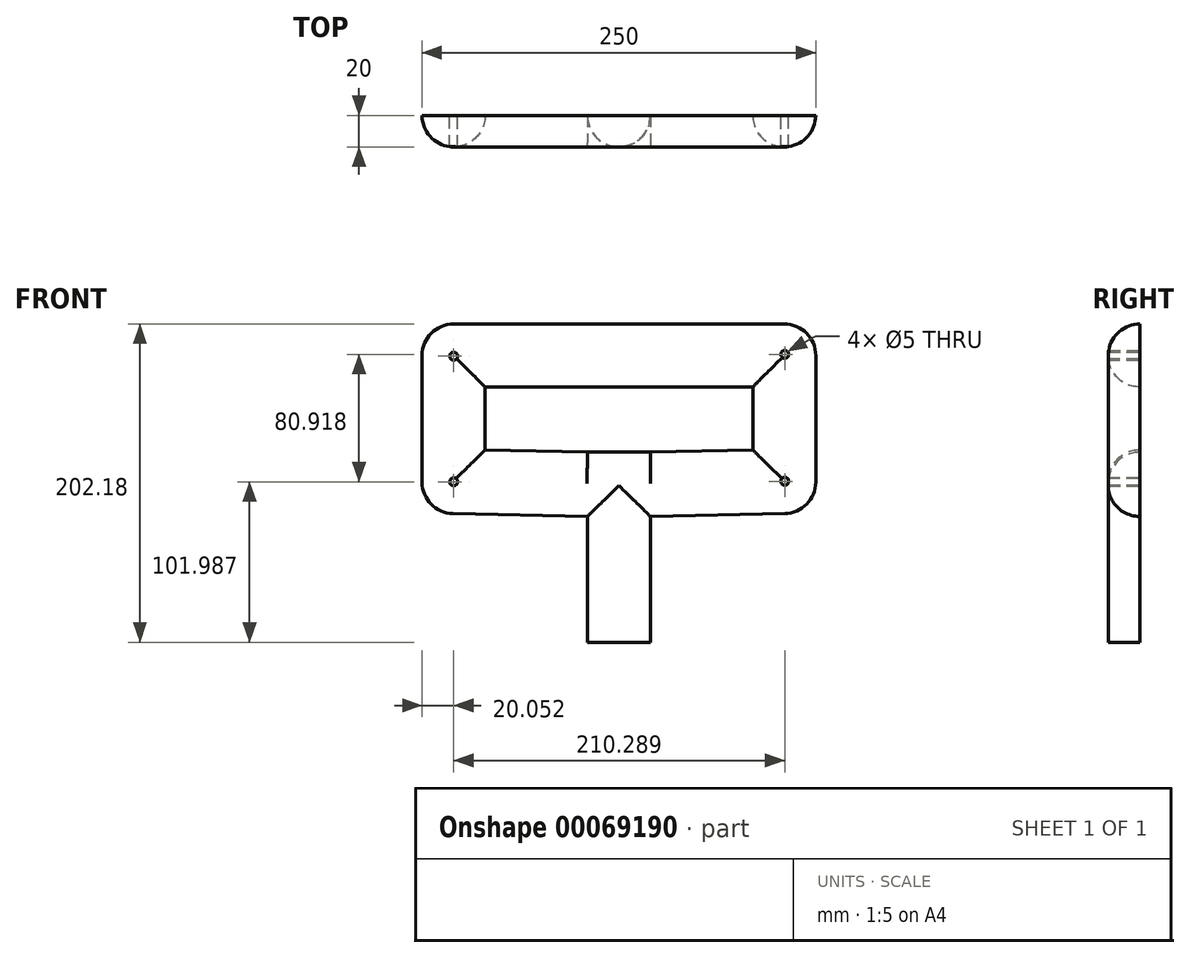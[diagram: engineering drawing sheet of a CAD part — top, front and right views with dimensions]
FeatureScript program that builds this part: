
annotation { "Feature Type Name" : "Feature", "Feature Type Description" : "" }
export const myFeature = defineFeature(function(context is Context, id is Id, definition is map)
    precondition{}
    {
        {
            var Q0;
            Q0=qCreatedBy(makeId("Front.planeOp"),FACE);
            var sketch = newSketch(context, id + "F0", { "sketchPlane" : qUnion([Q0])});
            skLineSegment(sketch, "E0", {"start": v(105, 80) * mm, "end": v(105, 0) * mm});
            skLineSegment(sketch, "E1", {"start": v(105, 0) * mm, "end": v(145, 0) * mm});
            skLineSegment(sketch, "E2", {"start": v(145, 0) * mm, "end": v(145, 80) * mm});
            skLineSegment(sketch, "E3", {"start": v(145, 80) * mm, "end": v(250, 82.18) * mm});
            skLineSegment(sketch, "E4", {"start": v(250, 82.18) * mm, "end": v(250, 202.18) * mm});
            skLineSegment(sketch, "E5", {"start": v(250, 202.18) * mm, "end": v(0, 202.18) * mm});
            skLineSegment(sketch, "E6", {"start": v(0, 202.18) * mm, "end": v(0, 82.18) * mm});
            skLineSegment(sketch, "E7", {"start": v(0, 82.18) * mm, "end": v(105, 80) * mm});
            skLineSegment(sketch, "E8", {"start": v(40, 162.18) * mm, "end": v(40, 122.18) * mm});
            skLineSegment(sketch, "E9", {"start": v(40, 122.18) * mm, "end": v(105, 120.83) * mm});
            skLineSegment(sketch, "E10", {"start": v(105, 120.83) * mm, "end": v(145, 120.83) * mm});
            skLineSegment(sketch, "E11", {"start": v(145, 120.83) * mm, "end": v(210, 122.18) * mm});
            skLineSegment(sketch, "E12", {"start": v(210, 122.18) * mm, "end": v(210, 162.18) * mm});
            skLineSegment(sketch, "E13", {"start": v(210, 162.18) * mm, "end": v(40, 162.18) * mm});
            skLineSegment(sketch, "E14", {"start": v(105, 80) * mm, "end": v(105, 120.83) * mm, "construction": true});
            skLineSegment(sketch, "E15", {"start": v(145, 80) * mm, "end": v(145, 120.83) * mm, "construction": true});
            skLineSegment(sketch, "E16", {"start": v(105, 80) * mm, "end": v(145, 80) * mm, "construction": true});
            skPoint(sketch, "E17", {"position": v(125, 162.18) * mm});
            skLineSegment(sketch, "E18", {"start": v(0, 82.18) * mm, "end": v(0, 0) * mm});
            skPoint(sketch, "E19", {"position": v(125, 202.18) * mm});
            skPoint(sketch, "E20", {"position": v(40, 142.18) * mm});
            skPoint(sketch, "E21", {"position": v(0, 142.18) * mm});
            skSolve(sketch);
        }
        {
            var Q0;
            Q0 = qSketchRegion(id + "F0", true);
            extrude(context, id + "F1", {"entities" : qUnion([Q0]), "depth" : 20 * mm});
        }
        {
            var Q0;
            Q0=makeQuery(id+"F1.opExtrude","CAP_EDGE",EDGE,{"disambiguationData":[OSD([sQuery(id+"F0.wireOp",EDGE,"E4")])],"isStart":false});
            var Q1;
            Q1=makeQuery(id+"F1.opExtrude","CAP_EDGE",EDGE,{"disambiguationData":[OSD([sQuery(id+"F0.wireOp",EDGE,"E6")])],"isStart":false});
            var Q2;
            Q2=makeQuery(id+"F1.opExtrude","CAP_EDGE",EDGE,{"disambiguationData":[OSD([sQuery(id+"F0.wireOp",EDGE,"E12")])],"isStart":false});
            var Q3;
            Q3=makeQuery(id+"F1.opExtrude","CAP_EDGE",EDGE,{"disambiguationData":[OSD([sQuery(id+"F0.wireOp",EDGE,"E13")])],"isStart":false});
            var Q4;
            Q4=makeQuery(id+"F1.opExtrude","CAP_EDGE",EDGE,{"disambiguationData":[OSD([sQuery(id+"F0.wireOp",EDGE,"E8")])],"isStart":false});
            var Q5;
            Q5=makeQuery(id+"F1.opExtrude","CAP_EDGE",EDGE,{"disambiguationData":[OSD([sQuery(id+"F0.wireOp",EDGE,"E0")])],"isStart":false});
            var Q6;
            Q6=makeQuery(id+"F1.opExtrude","CAP_EDGE",EDGE,{"disambiguationData":[OSD([sQuery(id+"F0.wireOp",EDGE,"E2")])],"isStart":false});
            fillet(context, id + "F2", {"entities" : qUnion([Q0, Q1, Q2, Q3, Q4, Q5, Q6]), "radius" : 20 * mm, "tangentPropagation" : true, "allowEdgeOverflow" : false});
        }
        {
            var Q0;
            Q0=makeQuery(id+"F1.opExtrude","CAP_EDGE",EDGE,{"disambiguationData":[OSD([sQuery(id+"F0.wireOp",EDGE,"E11")])],"isStart":false});
            var Q1;
            Q1=makeQuery(id+"F1.opExtrude","CAP_EDGE",EDGE,{"disambiguationData":[OSD([sQuery(id+"F0.wireOp",EDGE,"E9")])],"isStart":false});
            var Q2;
            Q2=makeQuery(id+"F1.opExtrude","CAP_EDGE",EDGE,{"disambiguationData":[OSD([sQuery(id+"F0.wireOp",EDGE,"E10")])],"isStart":false});
            var Q3;
            Q3=makeQuery(id+"F1.opExtrude","CAP_EDGE",EDGE,{"disambiguationData":[OSD([sQuery(id+"F0.wireOp",EDGE,"E7")])],"isStart":false});
            var Q4;
            Q4=makeQuery(id+"F1.opExtrude","CAP_EDGE",EDGE,{"disambiguationData":[OSD([sQuery(id+"F0.wireOp",EDGE,"E3")])],"isStart":false});
            var Q5;
            Q5=makeQuery(id+"F1.opExtrude","CAP_EDGE",EDGE,{"disambiguationData":[OSD([sQuery(id+"F0.wireOp",EDGE,"E5")])],"isStart":false});
            fillet(context, id + "F3", {"entities" : qUnion([Q0, Q1, Q2, Q3, Q4, Q5]), "radius" : 20 * mm, "tangentPropagation" : true, "allowEdgeOverflow" : false});
        }
        {
            var Q0;
            Q0=makeQuery(id+"F0.imprint","IMPRINT",FACE,{"disambiguationData":[TD([[makeQuery(id+"F0.imprint","IMPRINT",EDGE,{"derivedFrom":sQuery(id+"F0.wireOp",EDGE,"E0")}),1.0]])]});
            var sketch = newSketch(context, id + "F4", { "sketchPlane" : qUnion([Q0])});
            skLineSegment(sketch, "E22", {"start": v(40.1, 121.76) * mm, "end": v(0, 82.21) * mm, "construction": true});
            skPoint(sketch, "E23", {"position": v(20.05, 101.99) * mm});
            skLineSegment(sketch, "E24", {"start": v(249.93, 82.32) * mm, "end": v(210.75, 122.33) * mm, "construction": true});
            skLineSegment(sketch, "E25", {"start": v(0, 202.13) * mm, "end": v(38.88, 162.7) * mm, "construction": true});
            skLineSegment(sketch, "E26", {"start": v(249.87, 202.72) * mm, "end": v(209.36, 161.62) * mm, "construction": true});
            skPoint(sketch, "E27", {"position": v(230.34, 102.33) * mm});
            skPoint(sketch, "E28", {"position": v(230.34, 182.9) * mm});
            skPoint(sketch, "E29", {"position": v(20.05, 181.8) * mm});
            skSolve(sketch);
        }
        {
            var Q0;
            Q0=sQuery(id+"F4.wireOp",VERTEX,"E23");
            var Q1;
            Q1=sQuery(id+"F4.wireOp",VERTEX,"E29");
            var Q2;
            Q2=sQuery(id+"F4.wireOp",VERTEX,"E28");
            var Q3;
            Q3=sQuery(id+"F4.wireOp",VERTEX,"E27");
            var Q4;
            Q4=makeQuery(id+"F1.opExtrude","SWEPT_BODY",BODY,{"disambiguationData":[OSD([sQuery(id+"F0.wireOp",EDGE,"E0"),sQuery(id+"F0.wireOp",EDGE,"E1"),sQuery(id+"F0.wireOp",EDGE,"E2"),sQuery(id+"F0.wireOp",EDGE,"E3"),sQuery(id+"F0.wireOp",EDGE,"E4"),sQuery(id+"F0.wireOp",EDGE,"E5"),sQuery(id+"F0.wireOp",EDGE,"E6"),sQuery(id+"F0.wireOp",EDGE,"E7"),sQuery(id+"F0.wireOp",EDGE,"E8"),sQuery(id+"F0.wireOp",EDGE,"E9"),sQuery(id+"F0.wireOp",EDGE,"E10"),sQuery(id+"F0.wireOp",EDGE,"E11"),sQuery(id+"F0.wireOp",EDGE,"E12"),sQuery(id+"F0.wireOp",EDGE,"E13")])]});
            hole(context, id + "F5", {"style" : HoleStyle.SIMPLE, "holeDiameter" : 5 * mm, "endStyle" : HoleEndStyle.THROUGH, "oppositeDirection" : true, "locations" : qUnion([Q0, Q1, Q2, Q3]), "scope" : qUnion([Q4])});
        }
    });
